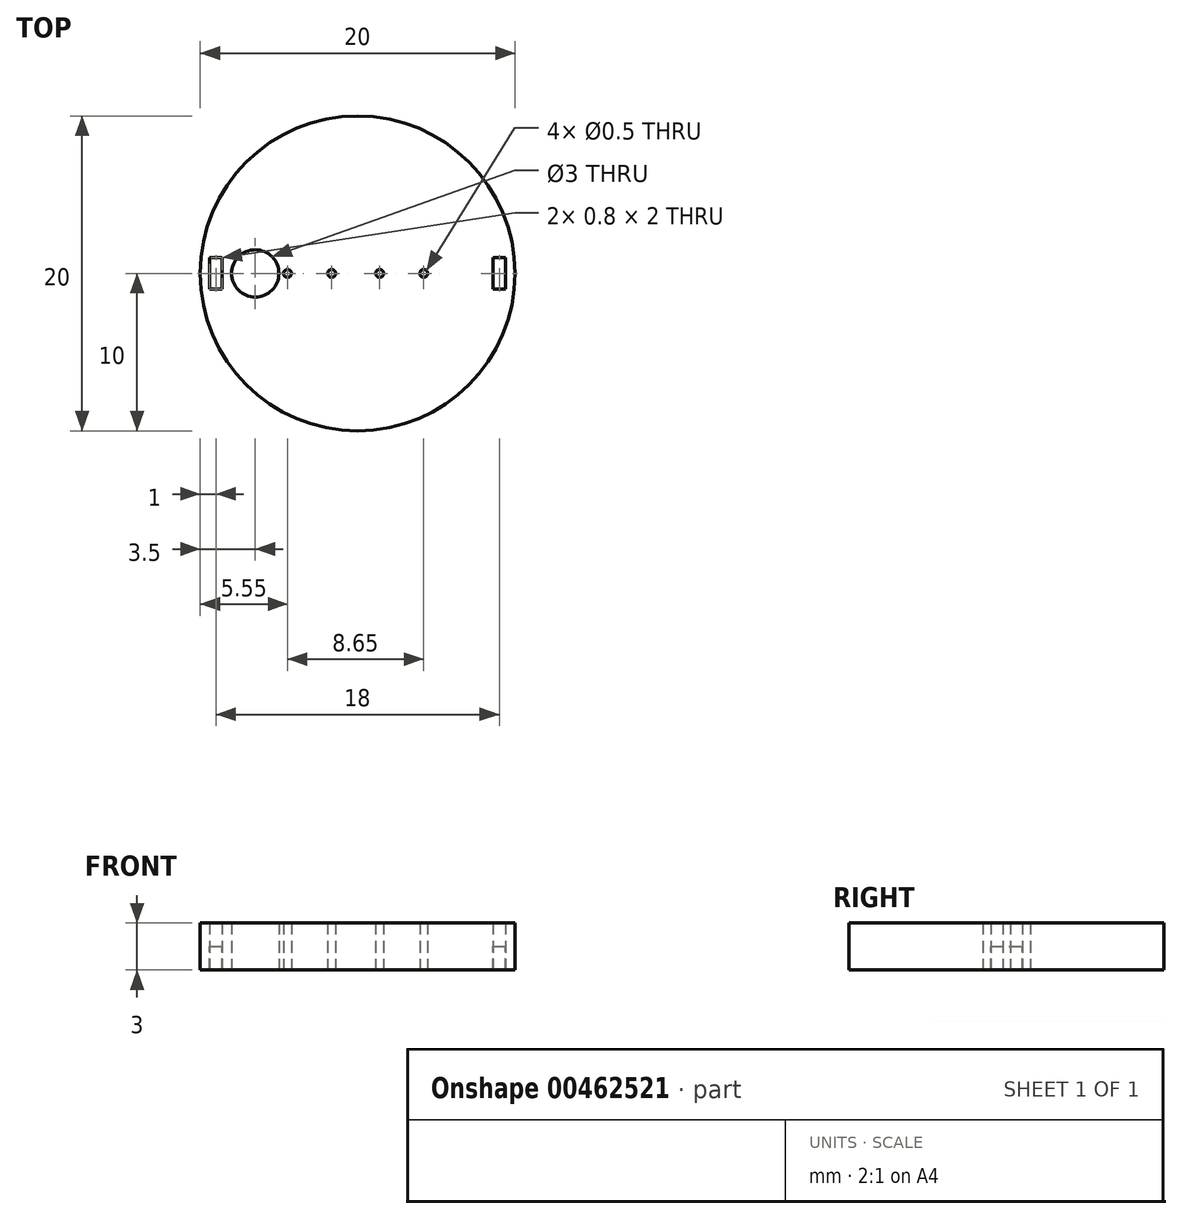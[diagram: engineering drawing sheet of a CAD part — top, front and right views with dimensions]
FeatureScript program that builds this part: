
annotation { "Feature Type Name" : "Feature", "Feature Type Description" : "" }
export const myFeature = defineFeature(function(context is Context, id is Id, definition is map)
    precondition{}
    {
        {
            var Q0;
            Q0=qCreatedBy(makeId("Top.planeOp"),FACE);
            var sketch = newSketch(context, id + "F0", { "sketchPlane" : qUnion([Q0])});
            skCircle(sketch, "E0", {"center": v(0, 0) * mm, "radius": 10 * mm});
            skCircle(sketch, "E1", {"center": v(-1.65, 0) * mm, "radius": 0.25 * mm});
            skCircle(sketch, "E2", {"center": v(1.4, 0) * mm, "radius": 0.25 * mm});
            skCircle(sketch, "E3", {"center": v(-6.5, 0) * mm, "radius": 1.5 * mm});
            skLineSegment(sketch, "E4.bottom", {"start": v(-9.4, -1) * mm, "end": v(-8.6, -1) * mm});
            skLineSegment(sketch, "E4.top", {"start": v(-9.4, 1) * mm, "end": v(-8.6, 1) * mm});
            skLineSegment(sketch, "E4.left", {"start": v(-9.4, -1) * mm, "end": v(-9.4, 1) * mm});
            skLineSegment(sketch, "E4.right", {"start": v(-8.6, -1) * mm, "end": v(-8.6, 1) * mm});
            skLineSegment(sketch, "E5.bottom", {"start": v(8.6, -1) * mm, "end": v(9.4, -1) * mm});
            skLineSegment(sketch, "E5.top", {"start": v(8.6, 1) * mm, "end": v(9.4, 1) * mm});
            skLineSegment(sketch, "E5.left", {"start": v(8.6, -1) * mm, "end": v(8.6, 1) * mm});
            skLineSegment(sketch, "E5.right", {"start": v(9.4, -1) * mm, "end": v(9.4, 1) * mm});
            skCircle(sketch, "E6", {"center": v(4.2, 0) * mm, "radius": 0.25 * mm});
            skCircle(sketch, "E7", {"center": v(-4.45, 0) * mm, "radius": 0.25 * mm});
            skSolve(sketch);
        }
        {
            var Q0;
            Q0=makeQuery(id+"F0.imprint","IMPRINT",FACE,{"disambiguationData":[TD([[makeQuery(id+"F0.imprint","IMPRINT",EDGE,{"derivedFrom":sQuery(id+"F0.wireOp",EDGE,"E4.bottom")}),1.0]])]});
            var Q1;
            Q1=makeQuery(id+"F0.imprint","IMPRINT",FACE,{"disambiguationData":[TD([[makeQuery(id+"F0.imprint","IMPRINT",EDGE,{"derivedFrom":sQuery(id+"F0.wireOp",EDGE,"E5.bottom")}),1.0]])]});
            extrude(context, id + "F1", {"entities" : qUnion([Q0, Q1]), "depth" : 0 * mm, "hasSecondDirection" : true, "secondDirectionOppositeDirection" : true, "secondDirectionDepth" : 1.5 * mm});
        }
        {
            var Q0;
            Q0=qSketchRegion(id+"F0",true);
            extrude(context, id + "F2", {"entities" : qUnion([Q0]), "depth" : 1.5 * mm, "hasSecondDirection" : true, "secondDirectionOppositeDirection" : true, "secondDirectionDepth" : 1.5 * mm});
        }
    });
